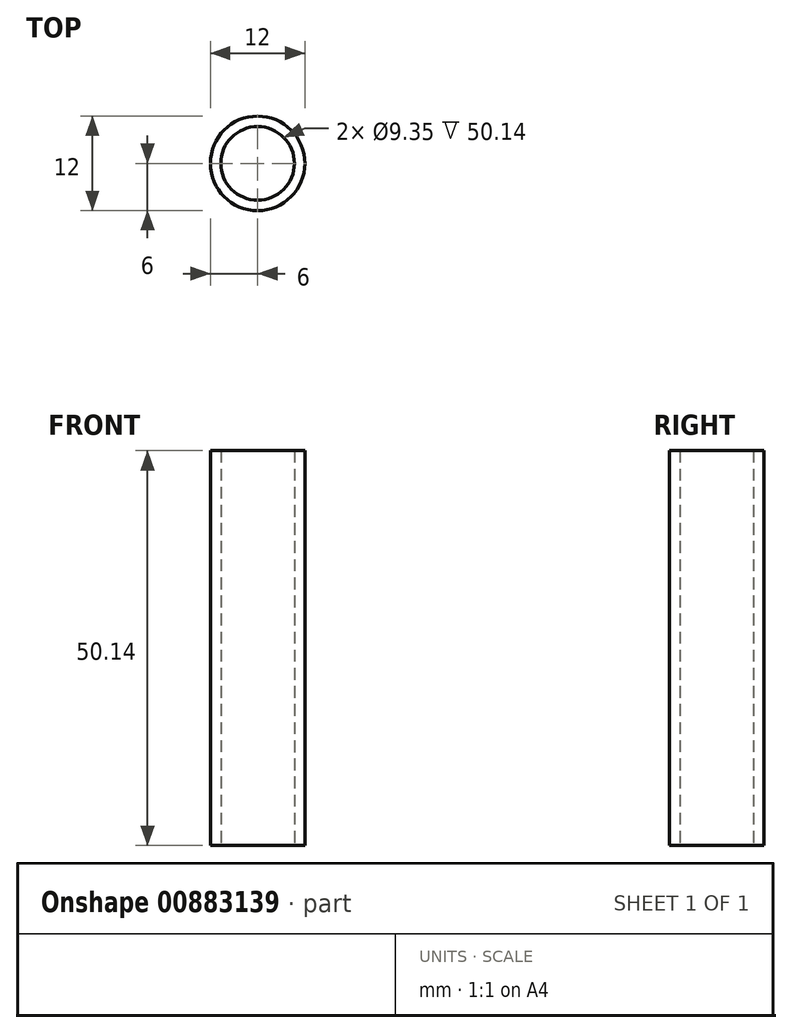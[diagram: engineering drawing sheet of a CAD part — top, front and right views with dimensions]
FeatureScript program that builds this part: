
annotation { "Feature Type Name" : "Feature", "Feature Type Description" : "" }
export const myFeature = defineFeature(function(context is Context, id is Id, definition is map)
    precondition{}
    {
        {
            var Q0;
            Q0=qCreatedBy(makeId("Top.planeOp"),FACE);
            var sketch = newSketch(context, id + "F0", { "sketchPlane" : qUnion([Q0])});
            skCircle(sketch, "E0", {"center": v(0, 0) * mm, "radius": 6 * mm});
            skCircle(sketch, "E1.0", {"center": v(0, 0) * mm, "radius": 4.68 * mm});
            skSolve(sketch);
        }
        {
            var Q0;
            Q0=qSketchRegion(id+"F0",true);
            extrude(context, id + "F1", {"entities" : qUnion([Q0]), "depth" : 50.14 * mm, "offsetDistance" : 25 * mm});
        }
    });
